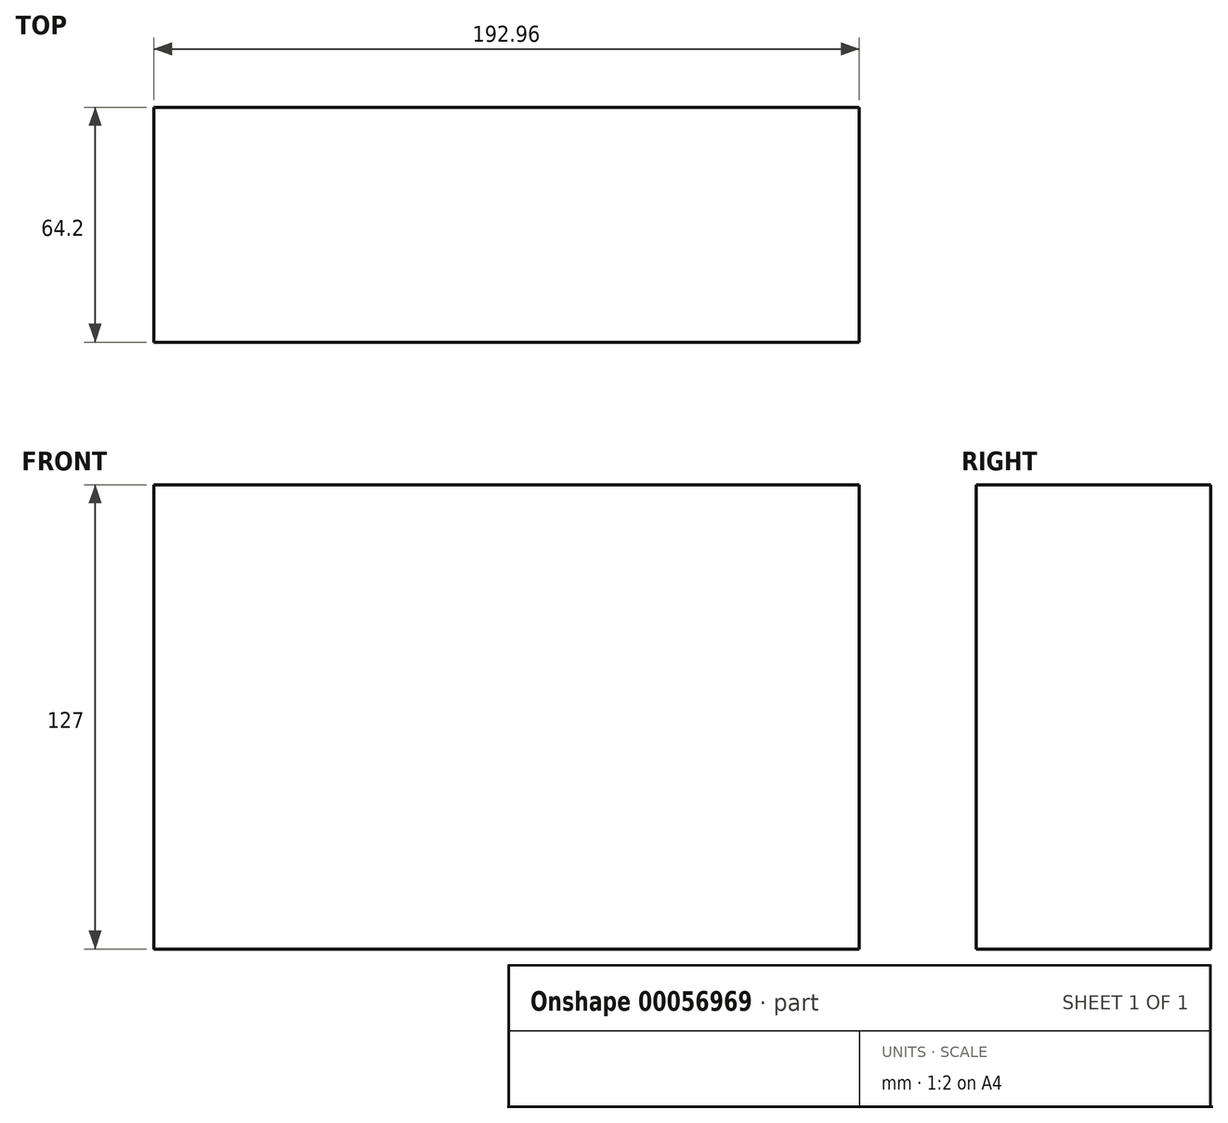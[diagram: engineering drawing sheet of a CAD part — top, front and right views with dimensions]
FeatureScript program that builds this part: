
annotation { "Feature Type Name" : "Feature", "Feature Type Description" : "" }
export const myFeature = defineFeature(function(context is Context, id is Id, definition is map)
    precondition{}
    {
        {
            var Q0;
            Q0=qCreatedBy(makeId("Top.planeOp"),FACE);
            var sketch = newSketch(context, id + "F0", { "sketchPlane" : qUnion([Q0])});
            skLineSegment(sketch, "E0.bottom", {"start": v(-134.06, -11.46) * mm, "end": v(58.9, -11.46) * mm});
            skLineSegment(sketch, "E0.top", {"start": v(-134.06, 52.74) * mm, "end": v(58.9, 52.74) * mm});
            skLineSegment(sketch, "E0.left", {"start": v(-134.06, -11.46) * mm, "end": v(-134.06, 52.74) * mm});
            skLineSegment(sketch, "E0.right", {"start": v(58.9, -11.46) * mm, "end": v(58.9, 52.74) * mm});
            skSolve(sketch);
        }
        {
            var Q0;
            Q0=makeQuery(id+"F0.imprint","IMPRINT",FACE,{"disambiguationData":[TD([[makeQuery(id+"F0.imprint","IMPRINT",EDGE,{"derivedFrom":sQuery(id+"F0.wireOp",EDGE,"E0.bottom")}),1.0]])]});
            extrude(context, id + "F1", {"entities" : qUnion([Q0]), "depth" : 127 * mm});
        }
    });
